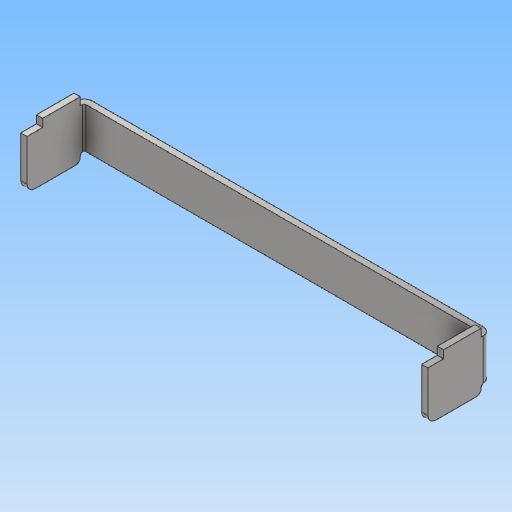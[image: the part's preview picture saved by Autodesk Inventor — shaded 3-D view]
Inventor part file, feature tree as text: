
AUTODESK INVENTOR PART (.ipt)
format: ipt  version: 2020 (Build 240168000, 168)  size: 271,360 bytes
history: native  units: mm
features: other x4, extrude x1
ambient origin geometry x8: Origin, YZ Plane, XZ Plane, XY Plane, X Axis, Y Axis, Z Axis, Center Point
bodies: Body1 (feature_tree)
feature tree (5):
  other  "實體1"
  extrude  "擠出1"  Depth=2.0mm TaperAngle=0.0deg
  other  "折彎零件1"
  other  "折彎零件2"
  other  "定義1"
